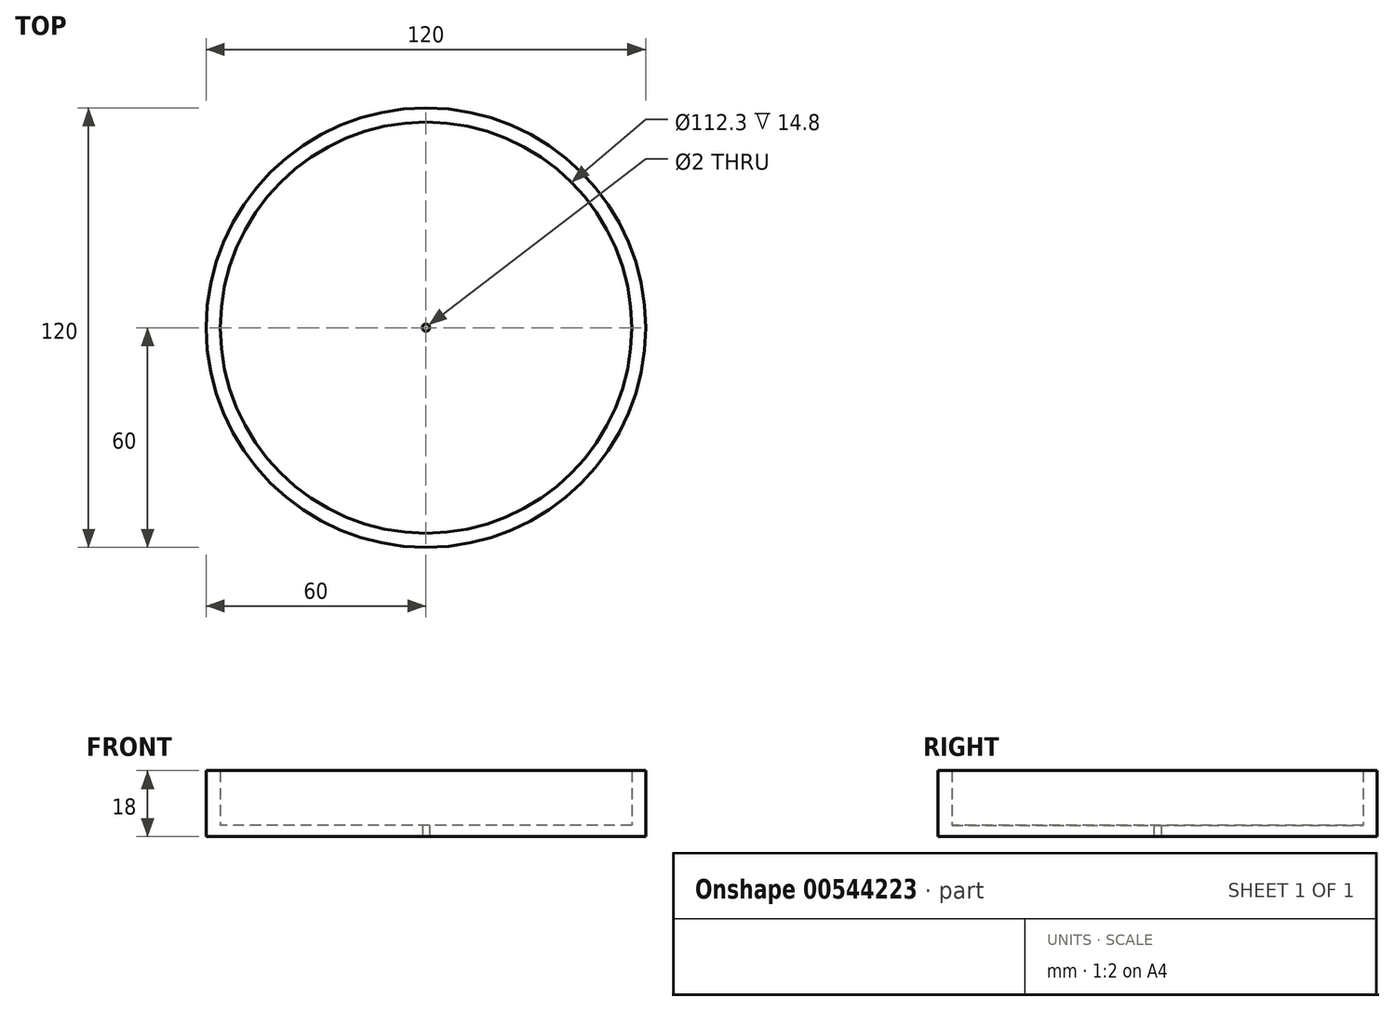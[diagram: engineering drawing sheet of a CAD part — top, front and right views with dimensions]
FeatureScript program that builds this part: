
annotation { "Feature Type Name" : "Feature", "Feature Type Description" : "" }
export const myFeature = defineFeature(function(context is Context, id is Id, definition is map)
    precondition{}
    {
        {
            var Q0;
            Q0=qCreatedBy(makeId("Top.planeOp"),FACE);
            var sketch = newSketch(context, id + "F0", { "sketchPlane" : qUnion([Q0])});
            skCircle(sketch, "E0", {"center": v(0, 0) * mm, "radius": 60 * mm});
            skSolve(sketch);
        }
        {
            var Q0;
            Q0=makeQuery(id+"F0.imprint","IMPRINT",FACE,{"disambiguationData":[TD([[makeQuery(id+"F0.imprint","IMPRINT",EDGE,{"derivedFrom":sQuery(id+"F0.wireOp",EDGE,"E0")}),1.0]])]});
            extrude(context, id + "F1", {"entities" : qUnion([Q0]), "depth" : 3 * mm, "offsetDistance" : 25 * mm});
        }
        {
            var Q0;
            Q0=makeQuery(id+"F1.opExtrude","CAP_FACE",FACE,{"disambiguationData":[OSD([sQuery(id+"F0.wireOp",EDGE,"E0")])],"isStart":false});
            var sketch = newSketch(context, id + "F2", { "sketchPlane" : qUnion([Q0])});
            skCircle(sketch, "E1", {"center": v(0, 0) * mm, "radius": 56.15 * mm});
            skSolve(sketch);
        }
        {
            var Q0;
            Q0=makeQuery(id+"F2.imprint","IMPRINT",FACE,{"disambiguationData":[TD([[makeQuery(id+"F2.imprint","IMPRINT",EDGE,{"derivedFrom":sQuery(id+"F2.wireOp",EDGE,"E1")}),-1.0]])]});
            extrude(context, id + "F3", {"entities" : qUnion([Q0]), "operationType" : NewBodyOperationType.ADD, "depth" : 15 * mm, "offsetDistance" : 25 * mm});
        }
        {
            var Q0;
            Q0=makeQuery(id+"F1.opExtrude","CAP_FACE",FACE,{"disambiguationData":[OSD([sQuery(id+"F0.wireOp",EDGE,"E0")])],"isStart":true});
            var sketch = newSketch(context, id + "F4", { "sketchPlane" : qUnion([Q0])});
            skPoint(sketch, "E2", {"position": v(0, 0) * mm});
            skSolve(sketch);
        }
        {
            var Q0;
            Q0=sQuery(id+"F4.wireOp",VERTEX,"E2");
            var Q1;
            Q1=makeQuery(id+"F1.opExtrude","SWEPT_BODY",BODY,{"disambiguationData":[OSD([sQuery(id+"F0.wireOp",EDGE,"E0")])]});
            hole(context, id + "F5", {"style" : HoleStyle.SIMPLE, "endStyle" : HoleEndStyle.THROUGH, "holeDiameter" : 2 * mm, "isTappedThrough" : true, "tappedDepth" : 12 * mm, "tapClearance" : 3, "locations" : qUnion([Q0]), "scope" : qUnion([Q1])});
        }
        {
            var Q0;
            Q0=makeQuery(id+"F3.opExtrude","CAP_EDGE",EDGE,{"disambiguationData":[OSD([sQuery(id+"F2.wireOp",EDGE,"E1")])],"isStart":false});
            fillet(context, id + "F6", {"entities" : qUnion([Q0]), "radius" : 0.2 * mm, "tangentPropagation" : true, "allowEdgeOverflow" : false});
        }
    });
